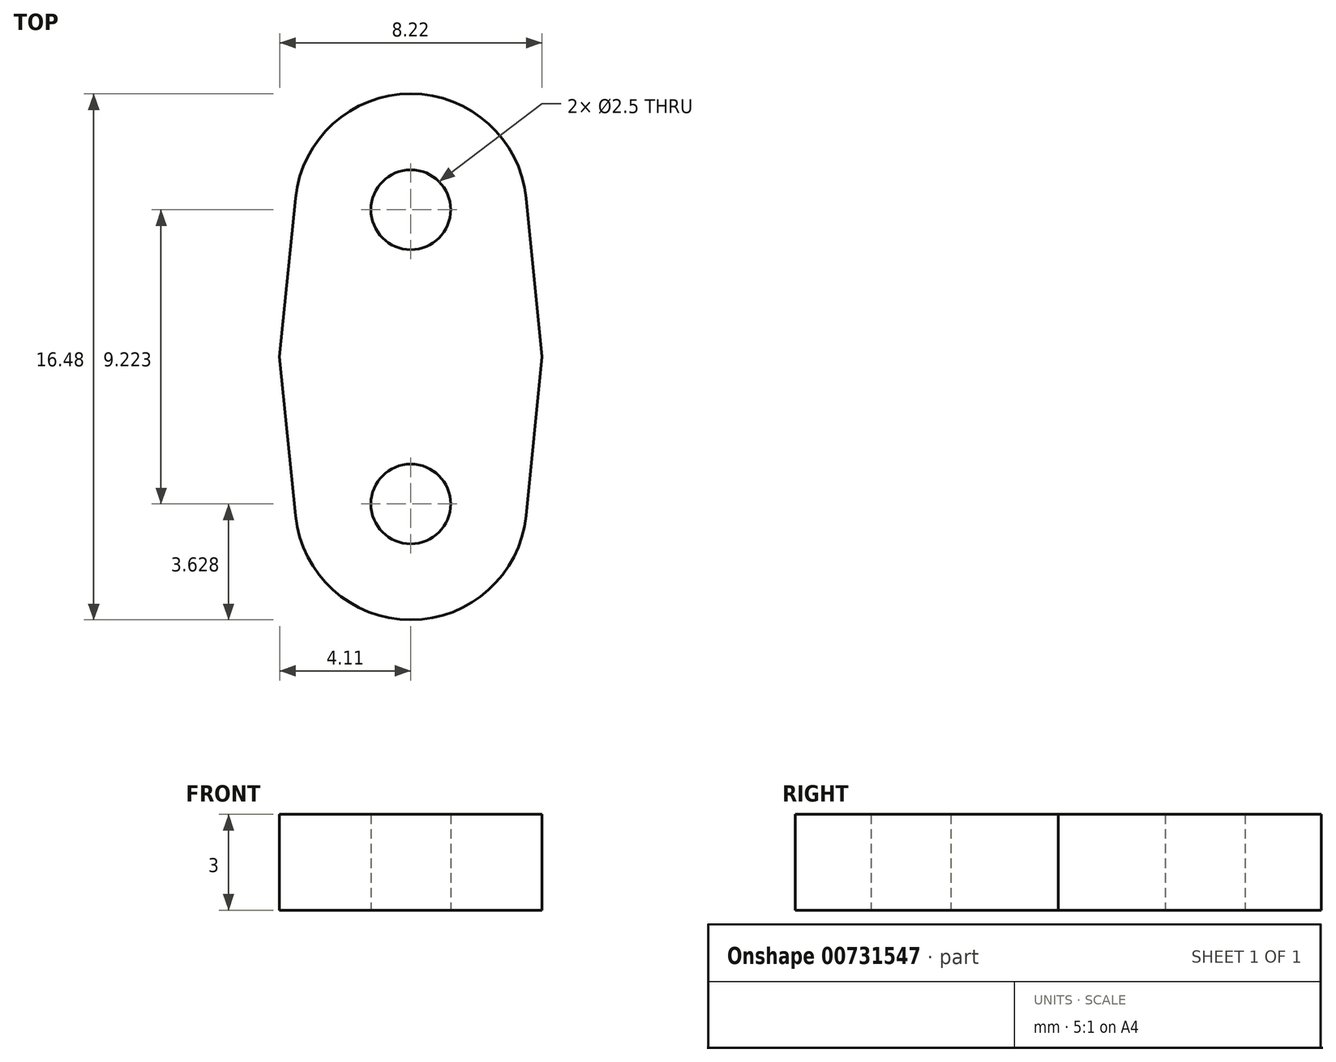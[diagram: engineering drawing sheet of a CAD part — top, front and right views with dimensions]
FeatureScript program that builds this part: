
annotation { "Feature Type Name" : "Feature", "Feature Type Description" : "" }
export const myFeature = defineFeature(function(context is Context, id is Id, definition is map)
    precondition{}
    {
        {
            var Q0;
            Q0=qCreatedBy(makeId("Top.planeOp"),FACE);
            var sketch = newSketch(context, id + "F0", { "sketchPlane" : qUnion([Q0])});
            skLineSegment(sketch, "E0", {"start": v(-4.11, 0) * mm, "end": v(-3.61, 4.97) * mm});
            skLineSegment(sketch, "E1", {"start": v(-4.11, 0) * mm, "end": v(-3.61, -4.97) * mm});
            skLineSegment(sketch, "E2", {"start": v(3.61, -4.97) * mm, "end": v(4.11, 0) * mm});
            skLineSegment(sketch, "E3", {"start": v(4.11, 0) * mm, "end": v(3.61, 4.97) * mm});
            skArc(sketch, "E4", {"start": v(3.61, 4.97) * mm, "mid": v(0, 8.24) * mm, "end": v(-3.61, 4.97) * mm});
            skArc(sketch, "E5", {"start": v(3.61, -4.97) * mm, "mid": v(0, -8.24) * mm, "end": v(-3.61, -4.97) * mm});
            skSolve(sketch);
        }
        {
            var Q0;
            Q0=makeQuery(id+"F0.imprint","IMPRINT",FACE,{"disambiguationData":[TD([[makeQuery(id+"F0.imprint","IMPRINT",EDGE,{"derivedFrom":sQuery(id+"F0.wireOp",EDGE,"E0")}),-1.0]])]});
            extrude(context, id + "F1", {"entities" : qUnion([Q0]), "depth" : 3 * mm, "offsetDistance" : 25 * mm});
        }
        {
            var Q0;
            Q0=sQuery(id+"F0.wireOp",VERTEX,"E4.center");
            var Q1;
            Q1=makeQuery(id+"F1.opExtrude","SWEPT_BODY",BODY,{"disambiguationData":[OSD([sQuery(id+"F0.wireOp",EDGE,"E0"),sQuery(id+"F0.wireOp",EDGE,"E1"),sQuery(id+"F0.wireOp",EDGE,"E2"),sQuery(id+"F0.wireOp",EDGE,"E3"),sQuery(id+"F0.wireOp",EDGE,"E4"),sQuery(id+"F0.wireOp",EDGE,"E5")])]});
            hole(context, id + "F2", {"style" : HoleStyle.SIMPLE, "endStyle" : HoleEndStyle.THROUGH, "oppositeDirection" : true, "holeDiameter" : 2.5 * mm, "majorDiameter" : 5 * mm, "isTappedThrough" : true, "tappedDepth" : 12 * mm, "tapClearance" : 3, "locations" : qUnion([Q0]), "scope" : qUnion([Q1])});
        }
        {
            var Q0;
            Q0=sQuery(id+"F0.wireOp",VERTEX,"E5.center");
            var Q1;
            Q1=makeQuery(id+"F1.opExtrude","SWEPT_BODY",BODY,{"disambiguationData":[OSD([sQuery(id+"F0.wireOp",EDGE,"E0"),sQuery(id+"F0.wireOp",EDGE,"E1"),sQuery(id+"F0.wireOp",EDGE,"E2"),sQuery(id+"F0.wireOp",EDGE,"E3"),sQuery(id+"F0.wireOp",EDGE,"E4"),sQuery(id+"F0.wireOp",EDGE,"E5")])]});
            hole(context, id + "F3", {"style" : HoleStyle.SIMPLE, "endStyle" : HoleEndStyle.THROUGH, "oppositeDirection" : true, "holeDiameter" : 2.5 * mm, "majorDiameter" : 5 * mm, "isTappedThrough" : true, "tappedDepth" : 12 * mm, "tapClearance" : 3, "locations" : qUnion([Q0]), "scope" : qUnion([Q1])});
        }
    });
